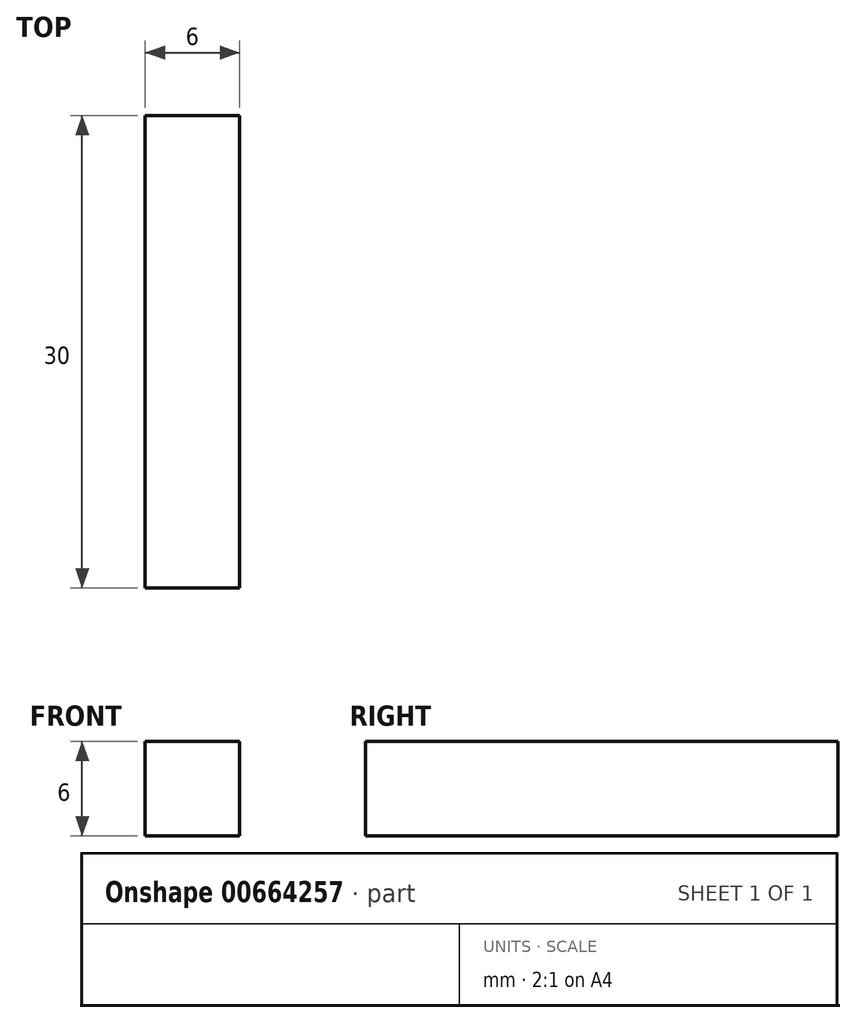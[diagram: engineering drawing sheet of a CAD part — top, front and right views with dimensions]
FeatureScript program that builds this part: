
annotation { "Feature Type Name" : "Feature", "Feature Type Description" : "" }
export const myFeature = defineFeature(function(context is Context, id is Id, definition is map)
    precondition{}
    {
        {
            var Q0;
            Q0=qCreatedBy(makeId("Front.planeOp"),FACE);
            var sketch = newSketch(context, id + "F0", { "sketchPlane" : qUnion([Q0])});
            skLineSegment(sketch, "E0.bottom", {"start": v(0, 0) * mm, "end": v(6, 0) * mm});
            skLineSegment(sketch, "E0.top", {"start": v(0, 6) * mm, "end": v(6, 6) * mm});
            skLineSegment(sketch, "E0.left", {"start": v(0, 0) * mm, "end": v(0, 6) * mm});
            skLineSegment(sketch, "E0.right", {"start": v(6, 0) * mm, "end": v(6, 6) * mm});
            skSolve(sketch);
        }
        {
            var Q0;
            Q0=makeQuery(id+"F0.imprint","IMPRINT",FACE,{"disambiguationData":[TD([[makeQuery(id+"F0.imprint","IMPRINT",EDGE,{"derivedFrom":sQuery(id+"F0.wireOp",EDGE,"E0.bottom")}),1.0]])]});
            extrude(context, id + "F1", {"entities" : qUnion([Q0]), "depth" : 30 * mm, "offsetDistance" : 25 * mm});
        }
    });
